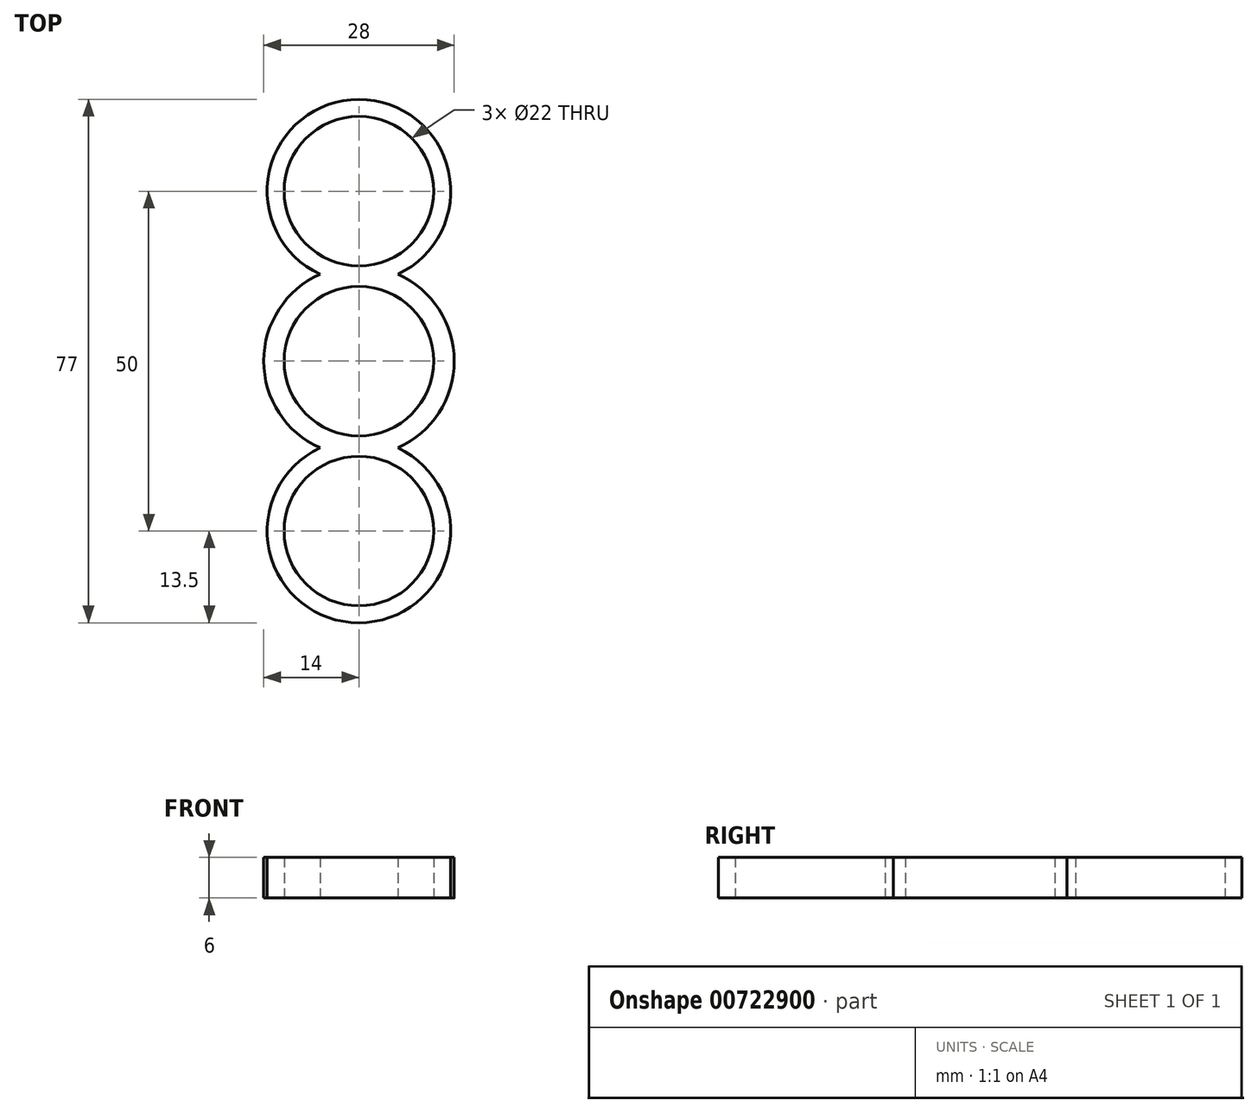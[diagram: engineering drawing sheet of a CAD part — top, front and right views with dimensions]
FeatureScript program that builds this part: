
annotation { "Feature Type Name" : "Feature", "Feature Type Description" : "" }
export const myFeature = defineFeature(function(context is Context, id is Id, definition is map)
    precondition{}
    {
        {
            var Q0;
            Q0=qCreatedBy(makeId("Top.planeOp"),FACE);
            var sketch = newSketch(context, id + "F0", { "sketchPlane" : qUnion([Q0])});
            skCircle(sketch, "E0", {"center": v(0, 0) * mm, "radius": 11 * mm});
            skLineSegment(sketch, "E1", {"start": v(0, 0) * mm, "end": v(0, 14) * mm});
            skCircle(sketch, "E2", {"center": v(0, 25) * mm, "radius": 11 * mm});
            skArc(sketch, "E3", {"start": v(5.73, 12.78) * mm, "mid": v(0, 38.5) * mm, "end": v(-5.73, 12.78) * mm});
            skArc(sketch, "E4", {"start": v(-5.73, 12.78) * mm, "mid": v(-14, 0) * mm, "end": v(-5.73, -12.78) * mm});
            skLineSegment(sketch, "E5", {"start": v(0, -11) * mm, "end": v(0, -25) * mm});
            skCircle(sketch, "E6", {"center": v(0, -25) * mm, "radius": 11 * mm});
            skArc(sketch, "E7", {"start": v(-5.73, -12.78) * mm, "mid": v(0, -38.5) * mm, "end": v(5.73, -12.78) * mm});
            skArc(sketch, "E8.trimOffspring", {"start": v(5.73, -12.78) * mm, "mid": v(14, 0) * mm, "end": v(5.73, 12.78) * mm});
            skSolve(sketch);
        }
        {
            var Q0;
            Q0=makeQuery(id+"F0.imprint","IMPRINT",FACE,{"disambiguationData":[TD([[makeQuery(id+"F0.imprint","IMPRINT",EDGE,{"derivedFrom":sQuery(id+"F0.wireOp",EDGE,"E2")}),-1.0]])]});
            extrude(context, id + "F1", {"entities" : qUnion([Q0]), "depth" : 6 * mm, "offsetDistance" : 25 * mm});
        }
    });
